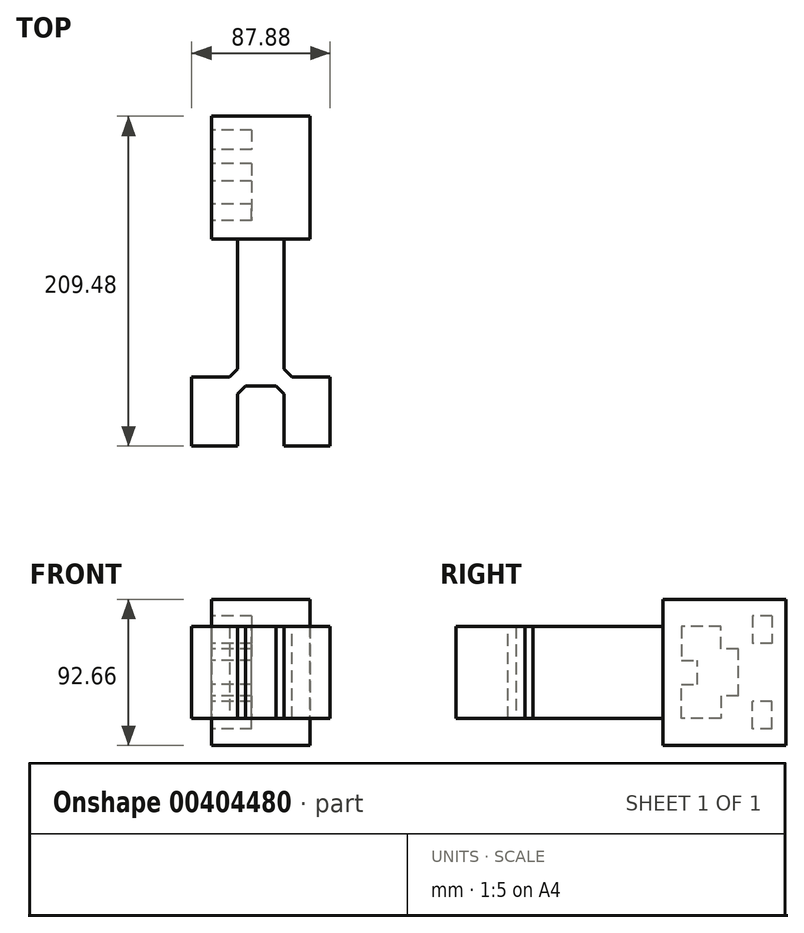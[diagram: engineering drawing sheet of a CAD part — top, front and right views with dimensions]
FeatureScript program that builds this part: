
annotation { "Feature Type Name" : "Feature", "Feature Type Description" : "" }
export const myFeature = defineFeature(function(context is Context, id is Id, definition is map)
    precondition{}
    {
        {
            var Q0;
            Q0=qCreatedBy(makeId("Top.planeOp"),FACE);
            var sketch = newSketch(context, id + "F0", { "sketchPlane" : qUnion([Q0])});
            skLineSegment(sketch, "E0", {"start": v(-43.94, -43.69) * mm, "end": v(-14.73, -43.69) * mm});
            skLineSegment(sketch, "E1", {"start": v(-14.73, -43.69) * mm, "end": v(-14.73, -5.59) * mm});
            skLineSegment(sketch, "E2", {"start": v(-14.73, -5.59) * mm, "end": v(0, -5.59) * mm});
            skLineSegment(sketch, "E3", {"start": v(-43.94, -43.69) * mm, "end": v(-43.94, 0) * mm});
            skLineSegment(sketch, "E4", {"start": v(-43.94, 0) * mm, "end": v(-14.73, 0) * mm});
            skLineSegment(sketch, "E5", {"start": v(-14.73, 0) * mm, "end": v(-14.73, 87.88) * mm});
            skLineSegment(sketch, "E6", {"start": v(-14.73, 87.88) * mm, "end": v(0, 87.88) * mm});
            skLineSegment(sketch, "E7", {"start": v(0, 70) * mm, "end": v(0, -60.34) * mm, "construction": true});
            skLineSegment(sketch, "E8.MirrorCS", {"start": v(14.73, 87.88) * mm, "end": v(0, 87.88) * mm});
            skLineSegment(sketch, "E9.MirrorCS", {"start": v(14.73, 0) * mm, "end": v(14.73, 87.88) * mm});
            skLineSegment(sketch, "E10.MirrorCS", {"start": v(43.94, 0) * mm, "end": v(14.73, 0) * mm});
            skLineSegment(sketch, "E11.MirrorCS", {"start": v(43.94, -43.69) * mm, "end": v(43.94, 0) * mm});
            skLineSegment(sketch, "E12.MirrorCS", {"start": v(43.94, -43.69) * mm, "end": v(14.73, -43.69) * mm});
            skLineSegment(sketch, "E13.MirrorCS", {"start": v(14.73, -43.69) * mm, "end": v(14.73, -5.59) * mm});
            skLineSegment(sketch, "E14.MirrorCS", {"start": v(14.73, -5.59) * mm, "end": v(0, -5.59) * mm});
            skSolve(sketch);
        }
        {
            var Q0;
            Q0 = qSketchRegion(id + "F0", true);
            extrude(context, id + "F1", {"entities" : qUnion([Q0]), "depth" : 58.42 * mm});
        }
        {
            var Q0;
            Q0=qCreatedBy(makeId("Right.planeOp"),FACE);
            var sketch = newSketch(context, id + "F2", { "sketchPlane" : qUnion([Q0])});
            skLineSegment(sketch, "E15", {"start": v(87.88, 58.42) * mm, "end": v(87.88, 0) * mm});
            skLineSegment(sketch, "E16", {"start": v(87.88, 0) * mm, "end": v(87.88, -17.12) * mm});
            skLineSegment(sketch, "E17", {"start": v(87.88, -17.12) * mm, "end": v(165.8, -17.12) * mm});
            skLineSegment(sketch, "E18", {"start": v(165.8, -17.12) * mm, "end": v(165.8, 75.54) * mm});
            skLineSegment(sketch, "E19", {"start": v(165.8, 75.54) * mm, "end": v(87.88, 75.54) * mm});
            skLineSegment(sketch, "E20", {"start": v(87.88, 75.54) * mm, "end": v(87.88, 54.58) * mm});
            skLineSegment(sketch, "E21", {"start": v(87.88, 29.21) * mm, "end": v(158.6, 29.21) * mm, "construction": true});
            skPoint(sketch, "E21.endSnap0", {"position": v(165.8, 29.21) * mm});
            skSolve(sketch);
        }
        {
            var Q0;
            {var subQ0=sQuery(id+"F2.wireOp",EDGE,"E15");Q0=makeQuery(id+"F2.imprint","IMPRINT",FACE,{"disambiguationData":[TD([[makeQuery(id+"F2.imprint","IMPRINT",EDGE,{"derivedFrom":subQ0}),1.0]])]});}
            extrude(context, id + "F3", {"entities" : qUnion([Q0]), "operationType" : NewBodyOperationType.ADD, "endBound" : BoundingType.SYMMETRIC, "depth" : 62.48 * mm});
        }
        {
            var Q0;
            Q0=makeQuery(id+"F3.opExtrude","CAP_FACE",FACE,{"disambiguationData":[OSD([sQuery(id+"F2.wireOp",EDGE,"E15"),sQuery(id+"F2.wireOp",EDGE,"E16"),sQuery(id+"F2.wireOp",EDGE,"E17"),sQuery(id+"F2.wireOp",EDGE,"E18"),sQuery(id+"F2.wireOp",EDGE,"E19"),sQuery(id+"F2.wireOp",EDGE,"E20")])],"isStart":true});
            var sketch = newSketch(context, id + "F4", { "sketchPlane" : qUnion([Q0])});
            skLineSegment(sketch, "E22", {"start": v(-165.8, 29.21) * mm, "end": v(-87.88, 29.21) * mm, "construction": true});
            skLineSegment(sketch, "E23.bottom", {"start": v(-157.1, -6.77) * mm, "end": v(-144.59, -6.77) * mm});
            skLineSegment(sketch, "E23.top", {"start": v(-157.1, 10.9) * mm, "end": v(-144.59, 10.9) * mm});
            skLineSegment(sketch, "E23.left", {"start": v(-157.1, -6.77) * mm, "end": v(-157.1, 10.9) * mm});
            skLineSegment(sketch, "E23.right", {"start": v(-144.59, -6.77) * mm, "end": v(-144.59, 10.9) * mm});
            skLineSegment(sketch, "E24", {"start": v(-135.57, 29.21) * mm, "end": v(-135.57, 14.2) * mm});
            skLineSegment(sketch, "E25", {"start": v(-135.57, 14.2) * mm, "end": v(-124.65, 14.2) * mm});
            skLineSegment(sketch, "E26", {"start": v(-124.65, 14.2) * mm, "end": v(-124.65, 0) * mm});
            skLineSegment(sketch, "E27", {"start": v(-124.65, 0) * mm, "end": v(-99.54, 0) * mm});
            skLineSegment(sketch, "E28", {"start": v(-99.54, 0) * mm, "end": v(-99.54, 21.53) * mm});
            skLineSegment(sketch, "E29", {"start": v(-99.54, 21.53) * mm, "end": v(-109.82, 21.53) * mm});
            skLineSegment(sketch, "E30", {"start": v(-109.82, 21.53) * mm, "end": v(-109.82, 29.21) * mm});
            skLineSegment(sketch, "E31.MirrorCS", {"start": v(-157.1, 65.19) * mm, "end": v(-157.1, 47.51) * mm});
            skLineSegment(sketch, "E32.MirrorCS", {"start": v(-157.1, 65.19) * mm, "end": v(-144.59, 65.19) * mm});
            skLineSegment(sketch, "E33.MirrorCS", {"start": v(-157.1, 47.51) * mm, "end": v(-144.59, 47.51) * mm});
            skLineSegment(sketch, "E34.MirrorCS", {"start": v(-144.59, 65.19) * mm, "end": v(-144.59, 47.51) * mm});
            skLineSegment(sketch, "E35.MirrorCS", {"start": v(-135.57, 29.2) * mm, "end": v(-135.57, 44.22) * mm});
            skLineSegment(sketch, "E36.MirrorCS", {"start": v(-135.57, 44.22) * mm, "end": v(-124.65, 44.22) * mm});
            skLineSegment(sketch, "E37.MirrorCS", {"start": v(-124.65, 44.22) * mm, "end": v(-124.65, 58.42) * mm});
            skLineSegment(sketch, "E38.MirrorCS", {"start": v(-124.65, 58.42) * mm, "end": v(-99.54, 58.42) * mm});
            skLineSegment(sketch, "E39.MirrorCS", {"start": v(-99.54, 58.42) * mm, "end": v(-99.54, 36.89) * mm});
            skLineSegment(sketch, "E40.MirrorCS", {"start": v(-99.54, 36.89) * mm, "end": v(-109.82, 36.89) * mm});
            skLineSegment(sketch, "E41.MirrorCS", {"start": v(-109.82, 36.89) * mm, "end": v(-109.82, 29.2) * mm});
            skSolve(sketch);
        }
        {
            var Q0;
            Q0 = qSketchRegion(id + "F4", true);
            extrude(context, id + "F5", {"entities" : qUnion([Q0]), "operationType" : NewBodyOperationType.REMOVE, "oppositeDirection" : true, "depth" : 25.4 * mm});
        }
        {
            var Q0;
            Q0=makeQuery(id+"F1.opExtrude","SWEPT_EDGE",EDGE,{"disambiguationData":[OSD([sQuery(id+"F0.wireOp",EDGE,"E13.MirrorCS"),sQuery(id+"F0.wireOp",EDGE,"E14.MirrorCS")])]});
            var Q1;
            Q1=makeQuery(id+"F1.opExtrude","SWEPT_EDGE",EDGE,{"disambiguationData":[OSD([sQuery(id+"F0.wireOp",EDGE,"E1"),sQuery(id+"F0.wireOp",EDGE,"E2")])]});
            var Q2;
            Q2=makeQuery(id+"F1.opExtrude","SWEPT_EDGE",EDGE,{"disambiguationData":[OSD([sQuery(id+"F0.wireOp",EDGE,"E4"),sQuery(id+"F0.wireOp",EDGE,"E5")])]});
            var Q3;
            Q3=makeQuery(id+"F1.opExtrude","SWEPT_EDGE",EDGE,{"disambiguationData":[OSD([sQuery(id+"F0.wireOp",EDGE,"E9.MirrorCS"),sQuery(id+"F0.wireOp",EDGE,"E10.MirrorCS")])]});
            chamfer(context, id + "F6", {"entities" : qUnion([Q0, Q1, Q2, Q3]), "width" : 5.08 * mm, "tangentPropagation" : true});
        }
    });
